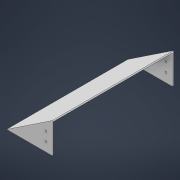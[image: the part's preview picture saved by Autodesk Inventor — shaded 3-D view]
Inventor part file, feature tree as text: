
AUTODESK INVENTOR PART (.ipt)
format: ipt  version: 2021 (Build 250183000, 183)  size: 258,048 bytes
history: native  units: mm
features: extrude x5, sketch x5, other x1
ambient origin geometry x8: Origin, YZ Plane, XZ Plane, XY Plane, X Axis, Y Axis, Z Axis, Center Point
bodies: Body1 (feature_tree)
feature tree (11):
  other  "Ebene3_vorne"
  extrude  "Extrusion2"  Depth=75.0mm
  extrude  "Extrusion3"  Depth=25.0mm
  extrude  "Extrusion4"  Depth=200.0mm TaperAngle=0.0deg
  extrude  "Extrusion5"  Depth=2.0mm TaperAngle=0.0deg
  extrude  "Extrusion6"  Depth=2.0mm
  sketch  "Skizze1"  dims[d0=50.0mm d1=75.0mm]
  sketch  "Skizze2"  dims[d2=25.0mm d3=25.0mm]
  sketch  "Skizze3"  dims[d4=2.0mm d7=200.0mm d8=0.0mm]
  sketch  "Skizze4"  dims[d9=2.0mm d10=0.0mm d11=2.0mm d12=0.0mm]
  sketch  "Skizze5"  dims[d13=3.2mm d14=3.2mm d15=15.0mm d16=15.0mm d17=10.0mm d18=10.0mm d19=2.0mm d20=0.0mm d21=3.2mm d22=3.2mm d23=10.0mm d24=10.0mm d25=15.0mm d26=15.0mm d27=2.0mm d28=0.0mm]
